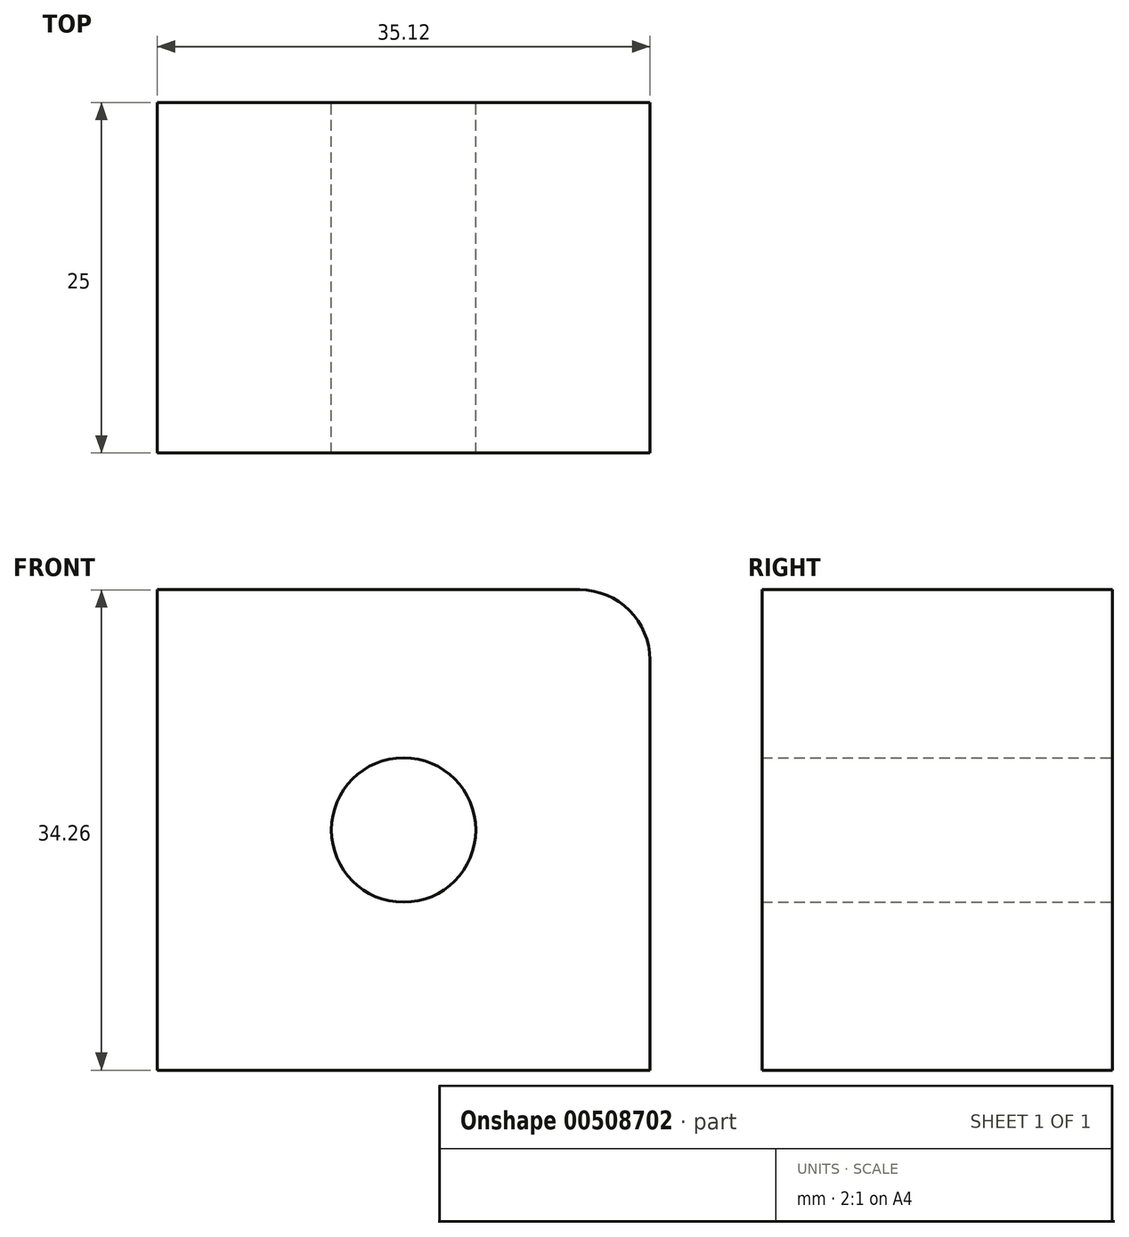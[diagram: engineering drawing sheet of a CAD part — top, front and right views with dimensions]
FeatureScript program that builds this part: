
annotation { "Feature Type Name" : "Feature", "Feature Type Description" : "" }
export const myFeature = defineFeature(function(context is Context, id is Id, definition is map)
    precondition{}
    {
        {
            var Q0;
            Q0=qCreatedBy(makeId("Front.planeOp"),FACE);
            var sketch = newSketch(context, id + "F0", { "sketchPlane" : qUnion([Q0])});
            skLineSegment(sketch, "E0.bottom", {"start": v(17.56, 17.13) * mm, "end": v(-17.56, 17.13) * mm});
            skLineSegment(sketch, "E0.top", {"start": v(17.56, -17.13) * mm, "end": v(-17.56, -17.13) * mm});
            skLineSegment(sketch, "E0.left", {"start": v(17.56, 17.13) * mm, "end": v(17.56, -17.13) * mm});
            skLineSegment(sketch, "E0.right", {"start": v(-17.56, 17.13) * mm, "end": v(-17.56, -17.13) * mm});
            skPoint(sketch, "E0.middle", {"position": v(0, 0) * mm});
            skSolve(sketch);
        }
        {
            var Q0;
            Q0=makeQuery(id+"F0.imprint","IMPRINT",FACE,{"disambiguationData":[TD([[makeQuery(id+"F0.imprint","IMPRINT",EDGE,{"derivedFrom":sQuery(id+"F0.wireOp",EDGE,"E0.bottom")}),1.0]])]});
            extrude(context, id + "F1", {"entities" : qUnion([Q0]), "depth" : 25 * mm, "offsetDistance" : 25 * mm});
        }
        {
            var Q0;
            Q0=makeQuery(id+"F1.opExtrude","SWEPT_EDGE",EDGE,{"disambiguationData":[OSD([sQuery(id+"F0.wireOp",EDGE,"E0.bottom"),sQuery(id+"F0.wireOp",EDGE,"E0.left")])]});
            fillet(context, id + "F2", {"entities" : qUnion([Q0]), "radius" : 5 * mm, "tangentPropagation" : true, "allowEdgeOverflow" : false});
        }
        {
            var Q0;
            Q0=sQuery(id+"F0.wireOp",VERTEX,"E0.middle");
            var Q1;
            Q1=makeQuery(id+"F1.opExtrude","SWEPT_BODY",BODY,{"disambiguationData":[OSD([sQuery(id+"F0.wireOp",EDGE,"E0.bottom"),sQuery(id+"F0.wireOp",EDGE,"E0.top"),sQuery(id+"F0.wireOp",EDGE,"E0.left"),sQuery(id+"F0.wireOp",EDGE,"E0.right")])]});
            hole(context, id + "F3", {"style" : HoleStyle.SIMPLE, "endStyle" : HoleEndStyle.THROUGH, "oppositeDirection" : true, "standardTappedOrClearance" : lookupTablePath({ "standard" : "ISO", "engagement" : "75%", "pitch" : "1.75 mm", "size" : "M12", "type" : "Tapped" }), "standardBlindInLast" : lookupTablePath({ "standard" : "ISO", "engagement" : "75%", "pitch" : "1.75 mm", "size" : "M12", "type" : "Tapped" }), "holeDiameter" : 10.3 * mm, "showTappedDepth" : true, "tappedDepth" : 12 * mm, "tapClearance" : 3, "startFromSketch" : true, "locations" : qUnion([Q0]), "scope" : qUnion([Q1]), "majorDiameter" : 12 * mm});
        }
    });
